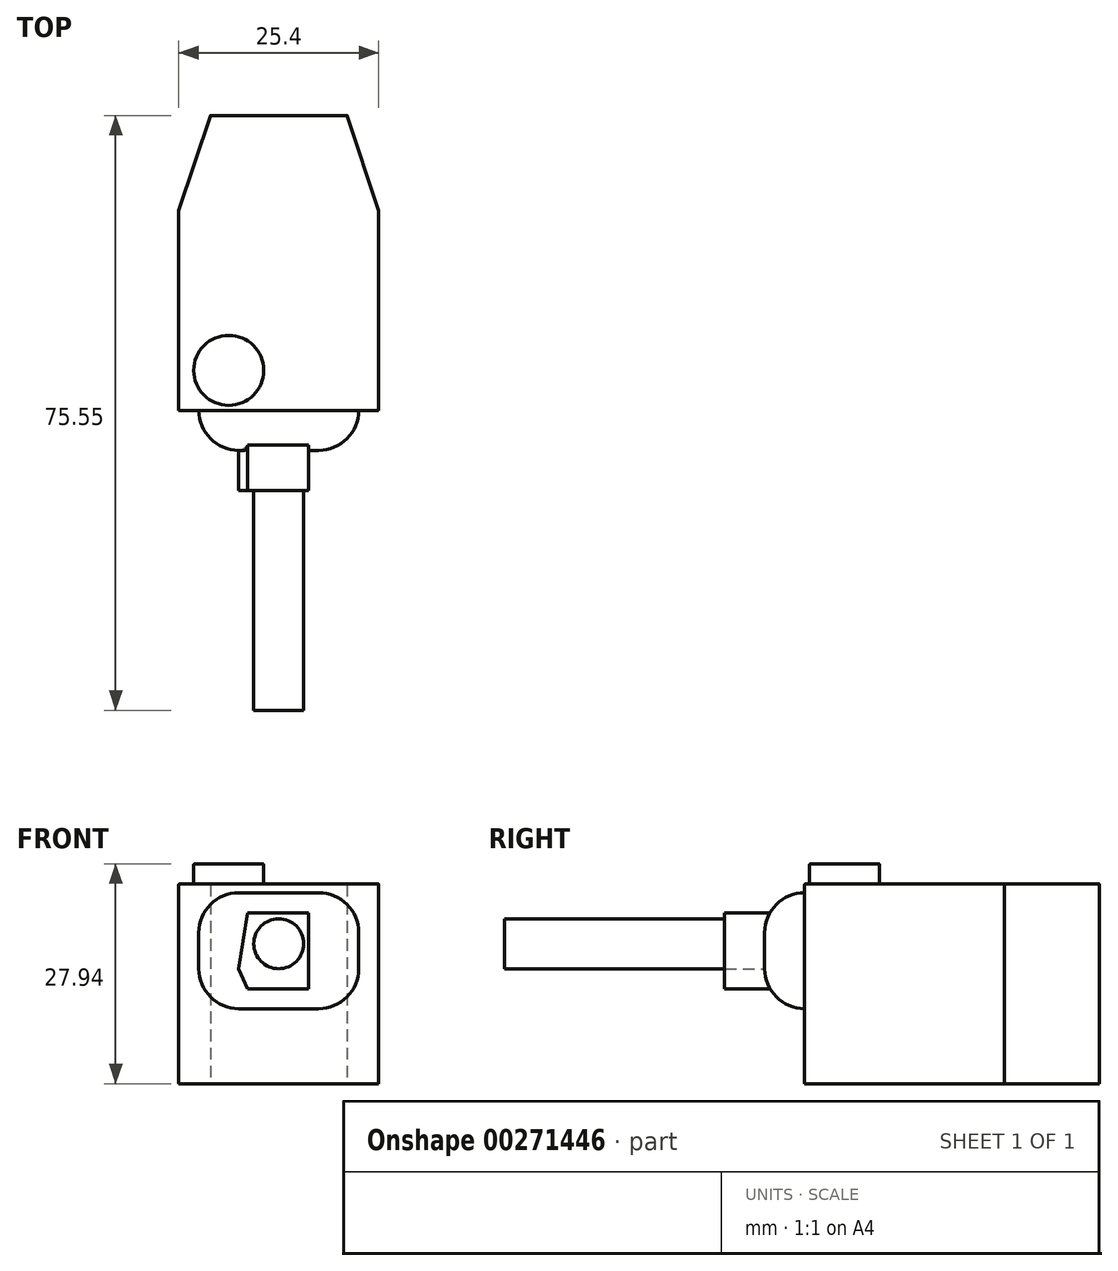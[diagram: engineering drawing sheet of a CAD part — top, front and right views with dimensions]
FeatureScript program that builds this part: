
annotation { "Feature Type Name" : "Feature", "Feature Type Description" : "" }
export const myFeature = defineFeature(function(context is Context, id is Id, definition is map)
    precondition{}
    {
        {
            var Q0;
            Q0=qCreatedBy(makeId("Top.planeOp"),FACE);
            var sketch = newSketch(context, id + "F0", { "sketchPlane" : qUnion([Q0])});
            skLineSegment(sketch, "E0", {"start": v(0, 0) * mm, "end": v(-12.7, 0) * mm});
            skLineSegment(sketch, "E1", {"start": v(0, 0) * mm, "end": v(12.7, 0) * mm});
            skLineSegment(sketch, "E2", {"start": v(12.7, 0) * mm, "end": v(12.7, 25.4) * mm});
            skLineSegment(sketch, "E3", {"start": v(12.7, 25.4) * mm, "end": v(8.68, 37.45) * mm});
            skLineSegment(sketch, "E4", {"start": v(8.68, 37.45) * mm, "end": v(-8.68, 37.45) * mm});
            skLineSegment(sketch, "E5", {"start": v(-12.7, 0) * mm, "end": v(-12.7, 25.4) * mm});
            skLineSegment(sketch, "E6", {"start": v(-12.7, 25.4) * mm, "end": v(-8.68, 37.45) * mm});
            skSolve(sketch);
        }
        {
            var Q0;
            Q0=makeQuery(id+"F0.imprint","IMPRINT",FACE,{"disambiguationData":[TD([[makeQuery(id+"F0.imprint","IMPRINT",EDGE,{"derivedFrom":sQuery(id+"F0.wireOp",EDGE,"E0")}),-1.0]])]});
            extrude(context, id + "F1", {"entities" : qUnion([Q0]), "depth" : 25.4 * mm});
        }
        {
            var Q0;
            Q0=makeQuery(id+"F1.opExtrude","CAP_FACE",FACE,{"disambiguationData":[OSD([sQuery(id+"F0.wireOp",EDGE,"E0"),sQuery(id+"F0.wireOp",EDGE,"E1"),sQuery(id+"F0.wireOp",EDGE,"E2"),sQuery(id+"F0.wireOp",EDGE,"E3"),sQuery(id+"F0.wireOp",EDGE,"E4"),sQuery(id+"F0.wireOp",EDGE,"E5"),sQuery(id+"F0.wireOp",EDGE,"E6")])],"isStart":false});
            var sketch = newSketch(context, id + "F2", { "sketchPlane" : qUnion([Q0])});
            skCircle(sketch, "E7", {"center": v(-6.35, 5.08) * mm, "radius": 4.45 * mm});
            skSolve(sketch);
        }
        {
            var Q0;
            Q0=makeQuery(id+"F2.imprint","IMPRINT",FACE,{"disambiguationData":[TD([[makeQuery(id+"F2.imprint","IMPRINT",EDGE,{"derivedFrom":sQuery(id+"F2.wireOp",EDGE,"E7")}),1.0]])]});
            extrude(context, id + "F3", {"entities" : qUnion([Q0]), "operationType" : NewBodyOperationType.ADD, "depth" : 2.54 * mm});
        }
        {
            var Q0;
            Q0=makeQuery(id+"F3.opExtrude","CAP_EDGE",EDGE,{"disambiguationData":[OSD([sQuery(id+"F2.wireOp",EDGE,"E7")])],"isStart":false});
            fillet(context, id + "F4", {"entities" : qUnion([Q0]), "radius" : 0.15 * mm, "tangentPropagation" : true, "allowEdgeOverflow" : false});
        }
        {
            var Q0;
            Q0=makeQuery(id+"F1.opExtrude","CAP_EDGE",EDGE,{"disambiguationData":[OSD([sQuery(id+"F0.wireOp",EDGE,"E2")])],"isStart":false});
            var Q1;
            Q1=makeQuery(id+"F1.opExtrude","CAP_EDGE",EDGE,{"disambiguationData":[OSD([sQuery(id+"F0.wireOp",EDGE,"E3")])],"isStart":false});
            var Q2;
            Q2=makeQuery(id+"F1.opExtrude","CAP_EDGE",EDGE,{"disambiguationData":[OSD([sQuery(id+"F0.wireOp",EDGE,"E4")])],"isStart":false});
            var Q3;
            Q3=makeQuery(id+"F1.opExtrude","CAP_EDGE",EDGE,{"disambiguationData":[OSD([sQuery(id+"F0.wireOp",EDGE,"E6")])],"isStart":false});
            var Q4;
            Q4=makeQuery(id+"F1.opExtrude","CAP_EDGE",EDGE,{"disambiguationData":[OSD([sQuery(id+"F0.wireOp",EDGE,"E5")])],"isStart":false});
            var Q5;
            Q5=makeQuery(id+"F1.opExtrude","CAP_EDGE",EDGE,{"disambiguationData":[OSD([sQuery(id+"F0.wireOp",EDGE,"E0"),sQuery(id+"F0.wireOp",EDGE,"E1")])],"isStart":false});
            fillet(context, id + "F5", {"entities" : qUnion([Q0, Q1, Q2, Q3, Q4, Q5]), "radius" : 0.13 * mm, "tangentPropagation" : true, "allowEdgeOverflow" : false});
        }
        {
            var Q0;
            Q0=makeQuery(id+"F1.opExtrude","SWEPT_FACE",FACE,{"disambiguationData":[OSD([sQuery(id+"F0.wireOp",EDGE,"E0"),sQuery(id+"F0.wireOp",EDGE,"E1")])]});
            var sketch = newSketch(context, id + "F6", { "sketchPlane" : qUnion([Q0])});
            skPoint(sketch, "E8.endSnap0", {"position": v(0, 25.27) * mm});
            skCircle(sketch, "E9", {"center": v(0, 17.78) * mm, "radius": 3.18 * mm});
            skSolve(sketch);
        }
        {
            var Q0;
            Q0=makeQuery(id+"F6.imprint","IMPRINT",FACE,{"disambiguationData":[TD([[makeQuery(id+"F6.imprint","IMPRINT",EDGE,{"derivedFrom":sQuery(id+"F6.wireOp",EDGE,"E9")}),1.0]])]});
            extrude(context, id + "F7", {"entities" : qUnion([Q0]), "operationType" : NewBodyOperationType.ADD, "depth" : 38.1 * mm});
        }
        {
            var Q0;
            Q0=makeQuery(id+"F1.opExtrude","SWEPT_FACE",FACE,{"disambiguationData":[OSD([sQuery(id+"F0.wireOp",EDGE,"E0"),sQuery(id+"F0.wireOp",EDGE,"E1")])]});
            var sketch = newSketch(context, id + "F8", { "sketchPlane" : qUnion([Q0])});
            skLineSegment(sketch, "E10", {"start": v(0, 14.6) * mm, "end": v(0, 12.06) * mm});
            skLineSegment(sketch, "E11", {"start": v(0, 12.06) * mm, "end": v(3.8, 12.06) * mm});
            skLineSegment(sketch, "E12", {"start": v(0, 12.06) * mm, "end": v(-3.94, 12.06) * mm});
            skLineSegment(sketch, "E13", {"start": v(-5.1, 14.6) * mm, "end": v(-3.94, 12.06) * mm});
            skLineSegment(sketch, "E14", {"start": v(0, 20.96) * mm, "end": v(0, 21.72) * mm});
            skLineSegment(sketch, "E15", {"start": v(0, 21.72) * mm, "end": v(3.8, 21.72) * mm});
            skLineSegment(sketch, "E16", {"start": v(0, 21.72) * mm, "end": v(-3.94, 21.72) * mm});
            skLineSegment(sketch, "E17", {"start": v(3.8, 21.72) * mm, "end": v(3.8, 12.06) * mm});
            skLineSegment(sketch, "E18", {"start": v(-3.94, 21.72) * mm, "end": v(-5.1, 14.6) * mm});
            skSolve(sketch);
        }
        {
            var Q0;
            Q0 = qSketchRegion(id + "F8", true);
            extrude(context, id + "F9", {"entities" : qUnion([Q0]), "operationType" : NewBodyOperationType.ADD, "depth" : 10.16 * mm});
        }
        {
            var Q0;
            Q0=makeQuery(id+"F1.opExtrude","SWEPT_FACE",FACE,{"disambiguationData":[OSD([sQuery(id+"F0.wireOp",EDGE,"E0"),sQuery(id+"F0.wireOp",EDGE,"E1")])]});
            var sketch = newSketch(context, id + "F10", { "sketchPlane" : qUnion([Q0])});
            skLineSegment(sketch, "E19", {"start": v(0, 24.26) * mm, "end": v(10.16, 24.26) * mm});
            skLineSegment(sketch, "E20", {"start": v(0, 24.26) * mm, "end": v(-10.16, 24.26) * mm});
            skLineSegment(sketch, "E21", {"start": v(0, 9.52) * mm, "end": v(10.16, 9.52) * mm});
            skLineSegment(sketch, "E22", {"start": v(10.16, 9.52) * mm, "end": v(10.16, 24.26) * mm});
            skLineSegment(sketch, "E23", {"start": v(0, 9.52) * mm, "end": v(-10.16, 9.52) * mm});
            skLineSegment(sketch, "E24", {"start": v(-10.16, 9.52) * mm, "end": v(-10.16, 24.26) * mm});
            skSolve(sketch);
        }
        {
            var Q0;
            Q0=makeQuery(id+"F10.imprint","IMPRINT",FACE,{"disambiguationData":[TD([[makeQuery(id+"F10.imprint","IMPRINT",EDGE,{"derivedFrom":makeQuery(id+"F9.opExtrude","CAP_EDGE",EDGE,{"disambiguationData":[OSD([sQuery(id+"F8.wireOp",EDGE,"E13")])],"isStart":true})}),1.0]])]});
            var Q1;
            Q1=makeQuery(id+"F10.imprint","IMPRINT",FACE,{"disambiguationData":[TD([[makeQuery(id+"F10.imprint","IMPRINT",EDGE,{"derivedFrom":sQuery(id+"F10.wireOp",EDGE,"E19")}),-1.0]])]});
            extrude(context, id + "F11", {"entities" : qUnion([Q0, Q1]), "operationType" : NewBodyOperationType.ADD, "depth" : 5.08 * mm});
        }
        {
            var Q0;
            Q0=makeQuery(id+"F11.opExtrude","CAP_EDGE",EDGE,{"disambiguationData":[OSD([sQuery(id+"F10.wireOp",EDGE,"E19"),sQuery(id+"F10.wireOp",EDGE,"E20")])],"isStart":false});
            var Q1;
            Q1=makeQuery(id+"F11.opExtrude","CAP_EDGE",EDGE,{"disambiguationData":[OSD([sQuery(id+"F10.wireOp",EDGE,"E21"),sQuery(id+"F10.wireOp",EDGE,"E23")])],"isStart":false});
            fillet(context, id + "F12", {"entities" : qUnion([Q0, Q1]), "radius" : 5.08 * mm, "tangentPropagation" : true, "allowEdgeOverflow" : false});
        }
        {
            var Q0;
            Q0=makeQuery(id+"F11.opExtrude","CAP_EDGE",EDGE,{"disambiguationData":[OSD([sQuery(id+"F10.wireOp",EDGE,"E22")])],"isStart":false});
            var Q1;
            Q1=makeQuery(id+"F11.opExtrude","CAP_EDGE",EDGE,{"disambiguationData":[OSD([sQuery(id+"F10.wireOp",EDGE,"E24")])],"isStart":false});
            fillet(context, id + "F13", {"entities" : qUnion([Q0, Q1]), "radius" : 5.08 * mm, "tangentPropagation" : true, "allowEdgeOverflow" : false});
        }
    });
